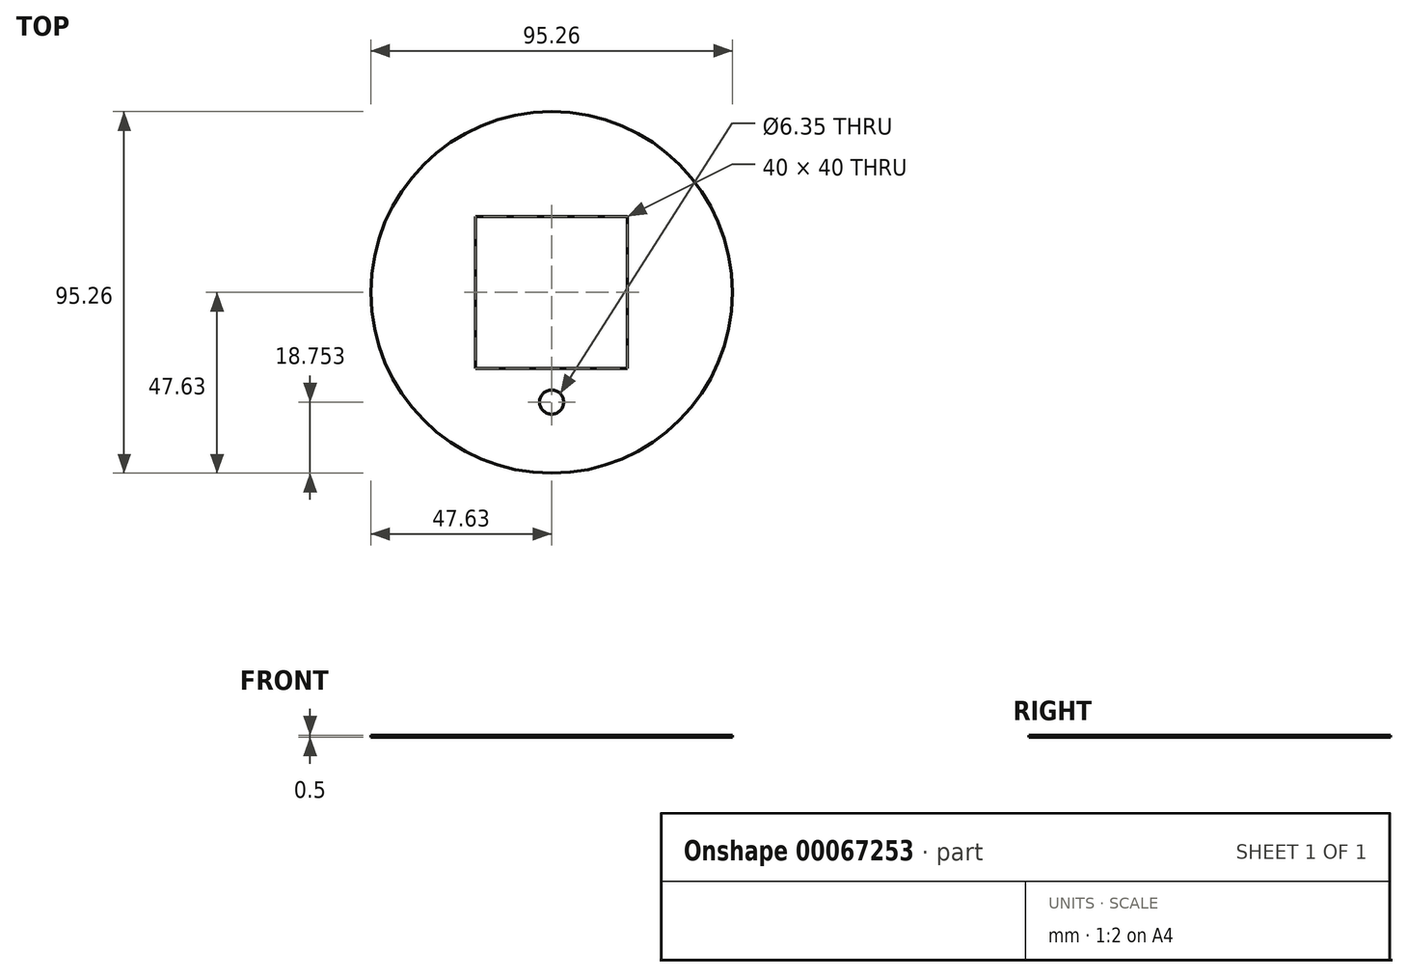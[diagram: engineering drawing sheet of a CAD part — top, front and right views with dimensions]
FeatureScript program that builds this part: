
annotation { "Feature Type Name" : "Feature", "Feature Type Description" : "" }
export const myFeature = defineFeature(function(context is Context, id is Id, definition is map)
    precondition{}
    {
        {
            var Q0;
            Q0=qCreatedBy(makeId("Top.planeOp"),FACE);
            var sketch = newSketch(context, id + "F0", { "sketchPlane" : qUnion([Q0])});
            skCircle(sketch, "E0", {"center": v(0, 0) * mm, "radius": 47.63 * mm});
            skLineSegment(sketch, "E1.bottom", {"start": v(-20, 20) * mm, "end": v(20, 20) * mm});
            skLineSegment(sketch, "E1.top", {"start": v(-20, -20) * mm, "end": v(20, -20) * mm});
            skLineSegment(sketch, "E1.left", {"start": v(-20, 20) * mm, "end": v(-20, -20) * mm});
            skLineSegment(sketch, "E1.right", {"start": v(20, 20) * mm, "end": v(20, -20) * mm});
            skCircle(sketch, "E2", {"center": v(0, -28.88) * mm, "radius": 3.18 * mm});
            skSolve(sketch);
        }
        {
            var Q0;
            Q0=qSketchRegion(id+"F0",true);
            extrude(context, id + "F1", {"entities" : qUnion([Q0]), "depth" : 0.5 * mm});
        }
    });
